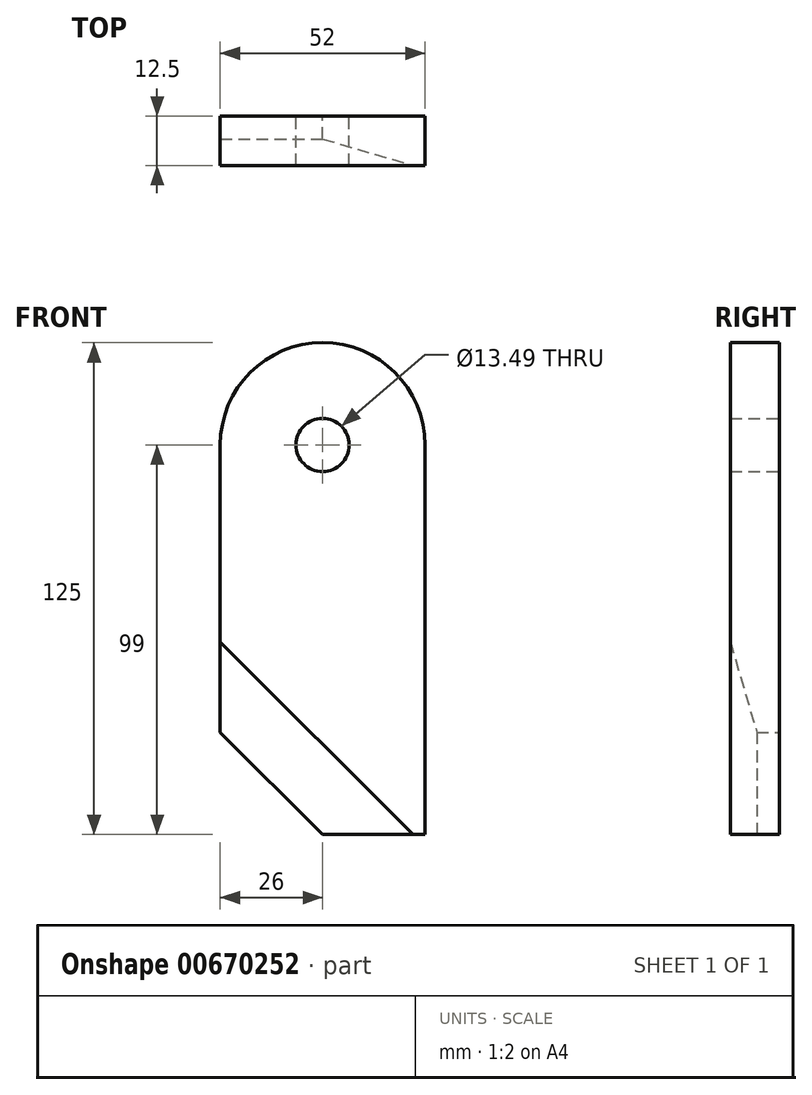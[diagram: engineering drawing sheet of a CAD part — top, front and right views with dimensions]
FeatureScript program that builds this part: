
annotation { "Feature Type Name" : "Feature", "Feature Type Description" : "" }
export const myFeature = defineFeature(function(context is Context, id is Id, definition is map)
    precondition{}
    {
        {
            var Q0;
            Q0=qCreatedBy(makeId("Front.planeOp"),FACE);
            var sketch = newSketch(context, id + "F0", { "sketchPlane" : qUnion([Q0])});
            skLineSegment(sketch, "E0.bottom", {"start": v(0, 26) * mm, "end": v(0, 26) * mm});
            skLineSegment(sketch, "E0.top", {"start": v(0, -99) * mm, "end": v(26, -99) * mm});
            skLineSegment(sketch, "E0.left", {"start": v(-26, 0) * mm, "end": v(-26, -73) * mm});
            skLineSegment(sketch, "E0.right", {"start": v(26, 0) * mm, "end": v(26, -99) * mm});
            skCircle(sketch, "E1", {"center": v(0, 0) * mm, "radius": 6.75 * mm});
            skLineSegment(sketch, "E2", {"start": v(-26, -73) * mm, "end": v(0, -99) * mm});
            skPoint(sketch, "E3.orphan", {"position": v(-26, -99) * mm});
            skPoint(sketch, "E4.visualSharp", {"position": v(-26, 26) * mm});
            skArc(sketch, "E4.filletArc", {"start": v(0, 26) * mm, "mid": v(-18.38, 18.38) * mm, "end": v(-26, 0) * mm});
            skPoint(sketch, "E5.visualSharp", {"position": v(26, 26) * mm});
            skArc(sketch, "E5.filletArc", {"start": v(26, 0) * mm, "mid": v(18.38, 18.38) * mm, "end": v(0, 26) * mm});
            skSolve(sketch);
        }
        {
            var Q0;
            Q0 = qSketchRegion(id + "F0", true);
            extrude(context, id + "F1", {"entities" : qUnion([Q0]), "endBound" : BoundingType.SYMMETRIC, "depth" : 12.5 * mm, "offsetDistance" : 25 * mm});
        }
        {
            var Q0;
            Q0=makeQuery(id+"F1.opExtrude","SWEPT_FACE",FACE,{"disambiguationData":[OSD([sQuery(id+"F0.wireOp",EDGE,"E0.top")])]});
            var sketch = newSketch(context, id + "F2", { "sketchPlane" : qUnion([Q0])});
            skPoint(sketch, "E6", {"position": v(0, -0.5) * mm});
            skSolve(sketch);
        }
        {
            var Q0;
            Q0=makeQuery(id+"F1.opExtrude","SWEPT_FACE",FACE,{"disambiguationData":[OSD([sQuery(id+"F0.wireOp",EDGE,"E0.left")])]});
            var sketch = newSketch(context, id + "F3", { "sketchPlane" : qUnion([Q0])});
            skPoint(sketch, "E7", {"position": v(-0.5, -73) * mm});
            skSolve(sketch);
        }
        {
            var Q0;
            Q0=makeQuery(id+"F1.opExtrude","CAP_FACE",FACE,{"disambiguationData":[OSD([sQuery(id+"F0.wireOp",EDGE,"E0.top"),sQuery(id+"F0.wireOp",EDGE,"E0.left"),sQuery(id+"F0.wireOp",EDGE,"E0.right"),sQuery(id+"F0.wireOp",EDGE,"E1"),sQuery(id+"F0.wireOp",EDGE,"E2"),sQuery(id+"F0.wireOp",EDGE,"E4.filletArc"),sQuery(id+"F0.wireOp",EDGE,"E5.filletArc")])],"isStart":false});
            var sketch = newSketch(context, id + "F4", { "sketchPlane" : qUnion([Q0])});
            skLineSegment(sketch, "E8", {"start": v(23, -99) * mm, "end": v(-26, -50) * mm});
            skPoint(sketch, "E9", {"position": v(-1.5, -74.5) * mm});
            skSolve(sketch);
        }
        {
            var Q0;
            Q0=sQuery(id+"F3.wireOp",VERTEX,"E7");
            var Q1;
            Q1=sQuery(id+"F4.wireOp",VERTEX,"E9");
            var Q2;
            Q2=sQuery(id+"F2.wireOp",VERTEX,"E6");
            cPlane(context, id + "F5", {"entities" : qUnion([Q0, Q1, Q2]), "cplaneType" : CPlaneType.THREE_POINT, "offset" : 25 * mm, "width" : 150 * mm, "height" : 150 * mm});
        }
        {
            var Q0;
            Q0=qCreatedBy(id+"F5.planeOp",FACE);
            var sketch = newSketch(context, id + "F6", { "sketchPlane" : qUnion([Q0])});
            skLineSegment(sketch, "E10.bottom", {"start": v(-23.71, -96.46) * mm, "end": v(34.71, -96.46) * mm});
            skLineSegment(sketch, "E10.top", {"start": v(-23.71, -34.61) * mm, "end": v(34.71, -34.61) * mm});
            skLineSegment(sketch, "E10.left", {"start": v(-23.71, -96.46) * mm, "end": v(-23.71, -34.61) * mm});
            skLineSegment(sketch, "E10.right", {"start": v(34.71, -96.46) * mm, "end": v(34.71, -34.61) * mm});
            skSolve(sketch);
        }
        {
            var Q0;
            Q0=makeQuery(id+"F6.imprint","IMPRINT",FACE,{"disambiguationData":[TD([[makeQuery(id+"F6.imprint","IMPRINT",EDGE,{"derivedFrom":sQuery(id+"F6.wireOp",EDGE,"E10.bottom")}),1.0]])]});
            extrude(context, id + "F7", {"entities" : qUnion([Q0]), "operationType" : NewBodyOperationType.REMOVE, "depth" : 25 * mm, "offsetDistance" : 25 * mm});
        }
    });
